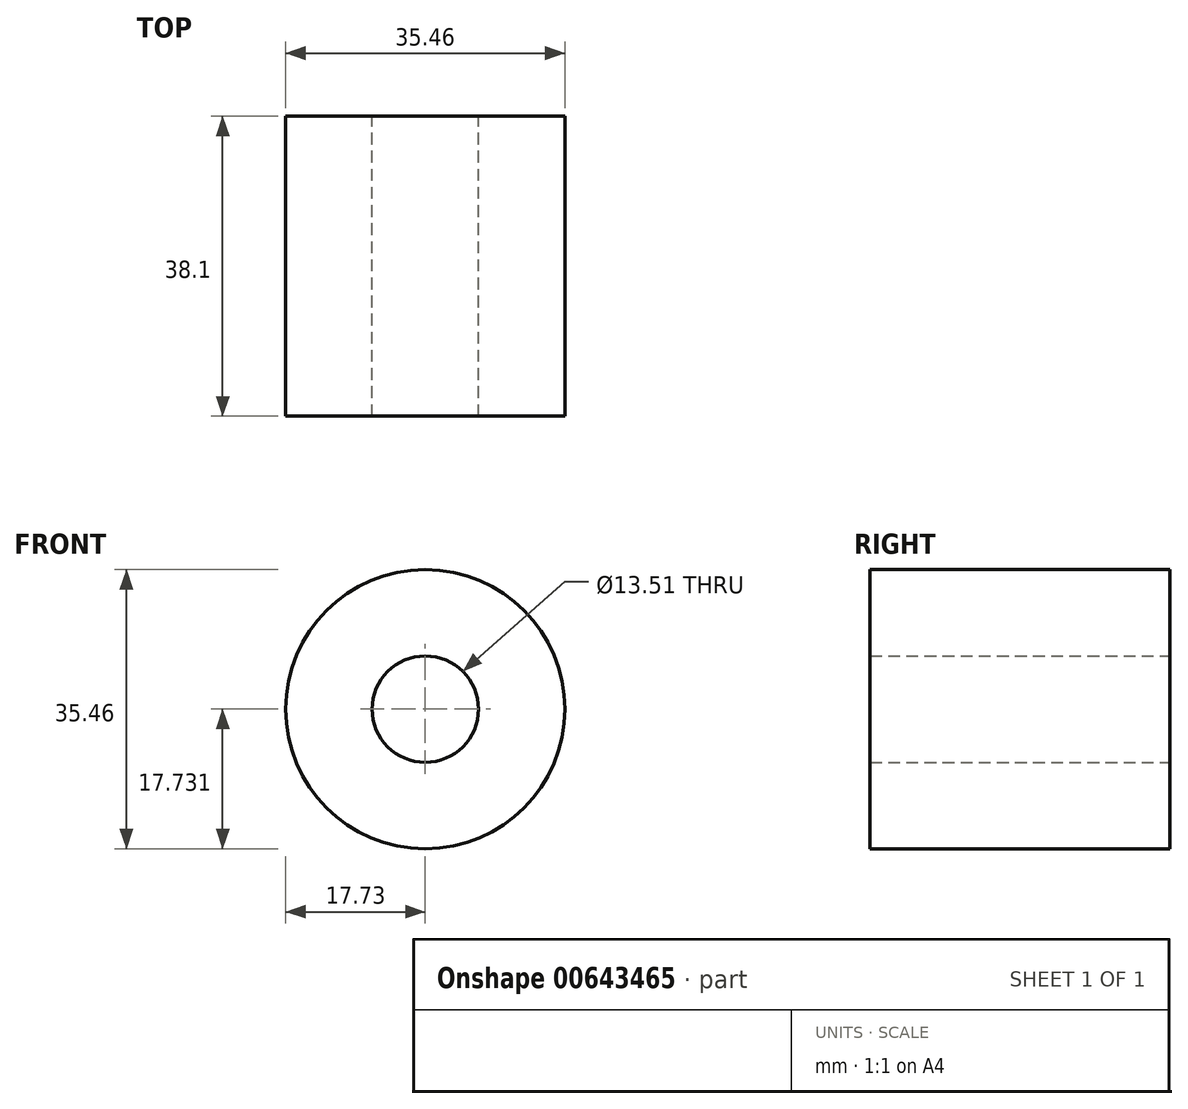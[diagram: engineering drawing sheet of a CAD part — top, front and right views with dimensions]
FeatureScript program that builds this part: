
annotation { "Feature Type Name" : "Feature", "Feature Type Description" : "" }
export const myFeature = defineFeature(function(context is Context, id is Id, definition is map)
    precondition{}
    {
        {
            var Q0;
            Q0=qCreatedBy(makeId("Front.planeOp"),FACE);
            var sketch = newSketch(context, id + "F0", { "sketchPlane" : qUnion([Q0])});
            skCircle(sketch, "E0", {"center": v(0, -2.83) * mm, "radius": 17.73 * mm});
            skCircle(sketch, "E1", {"center": v(0, -2.83) * mm, "radius": 6.76 * mm});
            skSolve(sketch);
        }
        {
            var Q0;
            Q0 = qSketchRegion(id + "F0", true);
            extrude(context, id + "F1", {"entities" : qUnion([Q0]), "depth" : 38.1 * mm, "offsetDistance" : 25.4 * mm});
        }
    });
